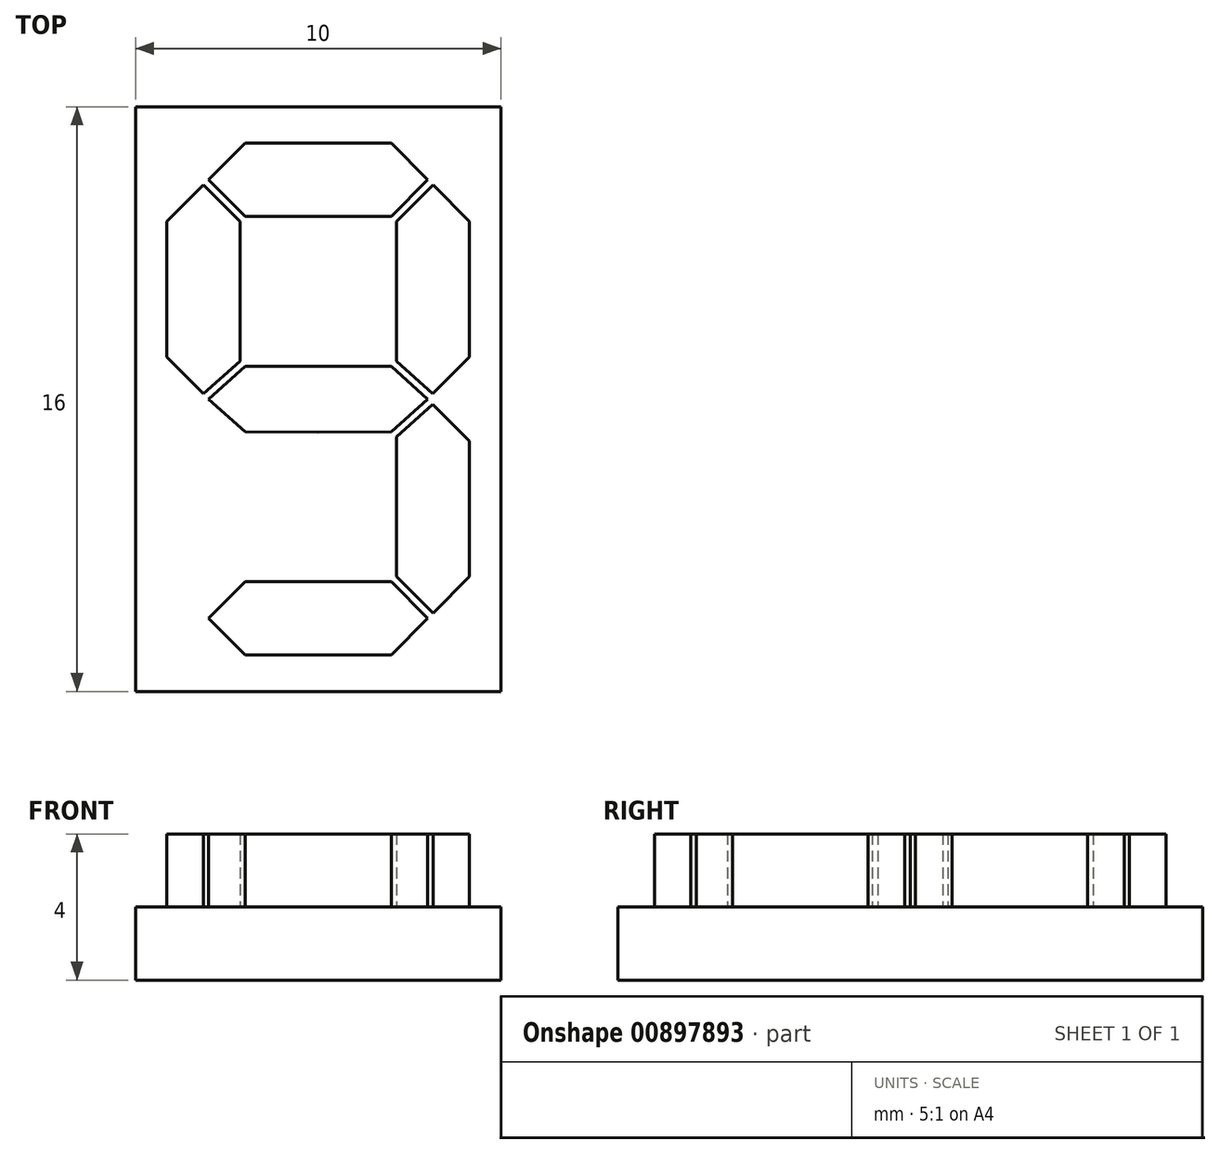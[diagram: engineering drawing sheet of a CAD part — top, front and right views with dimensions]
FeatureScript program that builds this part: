
annotation { "Feature Type Name" : "Feature", "Feature Type Description" : "" }
export const myFeature = defineFeature(function(context is Context, id is Id, definition is map)
    precondition{}
    {
        {
            var Q0;
            Q0=qCreatedBy(makeId("Top.planeOp"),FACE);
            var sketch = newSketch(context, id + "F0", { "sketchPlane" : qUnion([Q0])});
            skLineSegment(sketch, "E0.bottom", {"start": v(5, -8) * mm, "end": v(-5, -8) * mm});
            skLineSegment(sketch, "E0.top", {"start": v(5, 8) * mm, "end": v(-5, 8) * mm});
            skLineSegment(sketch, "E0.left", {"start": v(5, -8) * mm, "end": v(5, 8) * mm});
            skLineSegment(sketch, "E0.right", {"start": v(-5, -8) * mm, "end": v(-5, 8) * mm});
            skPoint(sketch, "E0.middle", {"position": v(0, 0) * mm});
            skSolve(sketch);
        }
        {
            var Q0;
            Q0=makeQuery(id+"F0.imprint","IMPRINT",FACE,{"disambiguationData":[TD([[makeQuery(id+"F0.imprint","IMPRINT",EDGE,{"derivedFrom":sQuery(id+"F0.wireOp",EDGE,"E0.bottom")}),-1.0]])]});
            extrude(context, id + "F1", {"entities" : qUnion([Q0]), "depth" : 2 * mm, "offsetDistance" : 25 * mm});
        }
        {
            var Q0;
            Q0=makeQuery(id+"F1.opExtrude","CAP_FACE",FACE,{"disambiguationData":[OSD([sQuery(id+"F0.wireOp",EDGE,"E0.bottom"),sQuery(id+"F0.wireOp",EDGE,"E0.top"),sQuery(id+"F0.wireOp",EDGE,"E0.left"),sQuery(id+"F0.wireOp",EDGE,"E0.right")])],"isStart":false});
            var sketch = newSketch(context, id + "F2", { "sketchPlane" : qUnion([Q0])});
            skLineSegment(sketch, "E1", {"start": v(-3, 8) * mm, "end": v(-3, -8) * mm, "construction": true});
            skLineSegment(sketch, "E2.0.1.0", {"start": v(-5, 6) * mm, "end": v(5, 6) * mm, "construction": true});
            skLineSegment(sketch, "E2.direction2", {"start": v(-5, 7) * mm, "end": v(-5, 6) * mm, "construction": true});
            skLineSegment(sketch, "E3.1.0.0", {"start": v(-2, 8) * mm, "end": v(-2, -8) * mm, "construction": true});
            skLineSegment(sketch, "E3.3.0.0", {"start": v(0, 8) * mm, "end": v(0, -8) * mm, "construction": true});
            skLineSegment(sketch, "E3.direction1", {"start": v(-3, -8) * mm, "end": v(-2, -8) * mm, "construction": true});
            skLineSegment(sketch, "E4", {"start": v(-2, 7) * mm, "end": v(-3, 6) * mm});
            skLineSegment(sketch, "E5", {"start": v(-3, 6) * mm, "end": v(-2, 5) * mm});
            skLineSegment(sketch, "E6", {"start": v(-2, 5) * mm, "end": v(0, 5) * mm});
            skLineSegment(sketch, "E7", {"start": v(-2, 7) * mm, "end": v(0, 7) * mm});
            skLineSegment(sketch, "E8.0", {"start": v(-3.14, 5.86) * mm, "end": v(-2.14, 4.86) * mm});
            skLineSegment(sketch, "E9", {"start": v(-2.14, 4.86) * mm, "end": v(-2.14, 1.03) * mm});
            skLineSegment(sketch, "E10.0", {"start": v(-4.14, 4.86) * mm, "end": v(-4.14, 1.15) * mm});
            skLineSegment(sketch, "E11", {"start": v(-3.14, 5.86) * mm, "end": v(-4.14, 4.86) * mm});
            skLineSegment(sketch, "E12", {"start": v(-4.14, 4.86) * mm, "end": v(5, 4.86) * mm, "construction": true});
            skLineSegment(sketch, "E13", {"start": v(0, 0.9) * mm, "end": v(-2, 0.9) * mm});
            skLineSegment(sketch, "E14", {"start": v(-2, 0.9) * mm, "end": v(-3, 0) * mm});
            skLineSegment(sketch, "E15.0", {"start": v(-2.14, 1.03) * mm, "end": v(-3.14, 0.15) * mm});
            skLineSegment(sketch, "E16", {"start": v(-3.14, 5.86) * mm, "end": v(-3.14, 0.15) * mm, "construction": true});
            skLineSegment(sketch, "E17", {"start": v(-4.14, 1.15) * mm, "end": v(-3.14, 0.15) * mm});
            skLineSegment(sketch, "E18.MirrorCS", {"start": v(0, -0.9) * mm, "end": v(-2, -0.9) * mm});
            skLineSegment(sketch, "E19.MirrorCS", {"start": v(-2, -0.9) * mm, "end": v(-3, 0) * mm});
            skLineSegment(sketch, "E20.MirrorCS", {"start": v(-2, -5) * mm, "end": v(0, -5) * mm});
            skLineSegment(sketch, "E21.MirrorCS", {"start": v(-3, -6) * mm, "end": v(-2, -5) * mm});
            skLineSegment(sketch, "E22.MirrorCS", {"start": v(-2, -7) * mm, "end": v(-3, -6) * mm});
            skLineSegment(sketch, "E23.MirrorCS", {"start": v(-2, -7) * mm, "end": v(0, -7) * mm});
            skLineSegment(sketch, "E24.MirrorCS", {"start": v(-3.14, -5.86) * mm, "end": v(-2.14, -4.86) * mm, "construction": true});
            skLineSegment(sketch, "E25.MirrorCS", {"start": v(-3.14, -5.86) * mm, "end": v(-4.14, -4.86) * mm, "construction": true});
            skLineSegment(sketch, "E26.MirrorCS", {"start": v(-4.14, -4.86) * mm, "end": v(-4.14, -1.15) * mm, "construction": true});
            skLineSegment(sketch, "E27.MirrorCS", {"start": v(-4.14, -1.15) * mm, "end": v(-3.14, -0.15) * mm, "construction": true});
            skLineSegment(sketch, "E28.MirrorCS", {"start": v(-2.14, -4.86) * mm, "end": v(-2.14, -1.03) * mm, "construction": true});
            skLineSegment(sketch, "E29.MirrorCS", {"start": v(-2.14, -1.03) * mm, "end": v(-3.14, -0.15) * mm, "construction": true});
            skLineSegment(sketch, "E30.MirrorCS", {"start": v(2, 7) * mm, "end": v(0, 7) * mm});
            skLineSegment(sketch, "E31.MirrorCS", {"start": v(2, 7) * mm, "end": v(3, 6) * mm});
            skLineSegment(sketch, "E32.MirrorCS", {"start": v(3, 6) * mm, "end": v(2, 5) * mm});
            skLineSegment(sketch, "E33.MirrorCS", {"start": v(2, 5) * mm, "end": v(0, 5) * mm});
            skLineSegment(sketch, "E34.MirrorCS", {"start": v(3.14, 5.86) * mm, "end": v(2.14, 4.86) * mm});
            skLineSegment(sketch, "E35.MirrorCS", {"start": v(3.14, 5.86) * mm, "end": v(4.14, 4.86) * mm});
            skLineSegment(sketch, "E36.MirrorCS", {"start": v(4.14, 4.86) * mm, "end": v(4.14, 1.15) * mm});
            skLineSegment(sketch, "E37.MirrorCS", {"start": v(4.14, 1.15) * mm, "end": v(3.14, 0.15) * mm});
            skLineSegment(sketch, "E38.MirrorCS", {"start": v(2.14, 4.86) * mm, "end": v(2.14, 1.03) * mm});
            skLineSegment(sketch, "E39.MirrorCS", {"start": v(2.14, 1.03) * mm, "end": v(3.14, 0.15) * mm});
            skLineSegment(sketch, "E40.MirrorCS", {"start": v(2, 0.9) * mm, "end": v(3, 0) * mm});
            skLineSegment(sketch, "E41.MirrorCS", {"start": v(0, 0.9) * mm, "end": v(2, 0.9) * mm});
            skLineSegment(sketch, "E42.MirrorCS", {"start": v(2, -0.9) * mm, "end": v(3, 0) * mm});
            skLineSegment(sketch, "E43.MirrorCS", {"start": v(0, -0.9) * mm, "end": v(2, -0.9) * mm});
            skLineSegment(sketch, "E44.MirrorCS", {"start": v(2.14, -1.03) * mm, "end": v(3.14, -0.15) * mm});
            skLineSegment(sketch, "E45.MirrorCS", {"start": v(4.14, -1.15) * mm, "end": v(3.14, -0.15) * mm});
            skLineSegment(sketch, "E46.MirrorCS", {"start": v(4.14, -4.86) * mm, "end": v(4.14, -1.15) * mm});
            skLineSegment(sketch, "E47.MirrorCS", {"start": v(2.14, -4.86) * mm, "end": v(2.14, -1.03) * mm});
            skLineSegment(sketch, "E48.MirrorCS", {"start": v(3.14, -5.86) * mm, "end": v(2.14, -4.86) * mm});
            skLineSegment(sketch, "E49.MirrorCS", {"start": v(3.14, -5.86) * mm, "end": v(4.14, -4.86) * mm});
            skLineSegment(sketch, "E50.MirrorCS", {"start": v(3, -6) * mm, "end": v(2, -5) * mm});
            skLineSegment(sketch, "E51.MirrorCS", {"start": v(2, -5) * mm, "end": v(0, -5) * mm});
            skLineSegment(sketch, "E52.MirrorCS", {"start": v(2, -7) * mm, "end": v(3, -6) * mm});
            skLineSegment(sketch, "E53.MirrorCS", {"start": v(2, -7) * mm, "end": v(0, -7) * mm});
            skSolve(sketch);
        }
        {
            var Q0;
            Q0=qSketchRegion(id+"F2",true);
            extrude(context, id + "F3", {"entities" : qUnion([Q0]), "operationType" : NewBodyOperationType.ADD, "depth" : 2 * mm, "offsetDistance" : 25 * mm});
        }
    });
